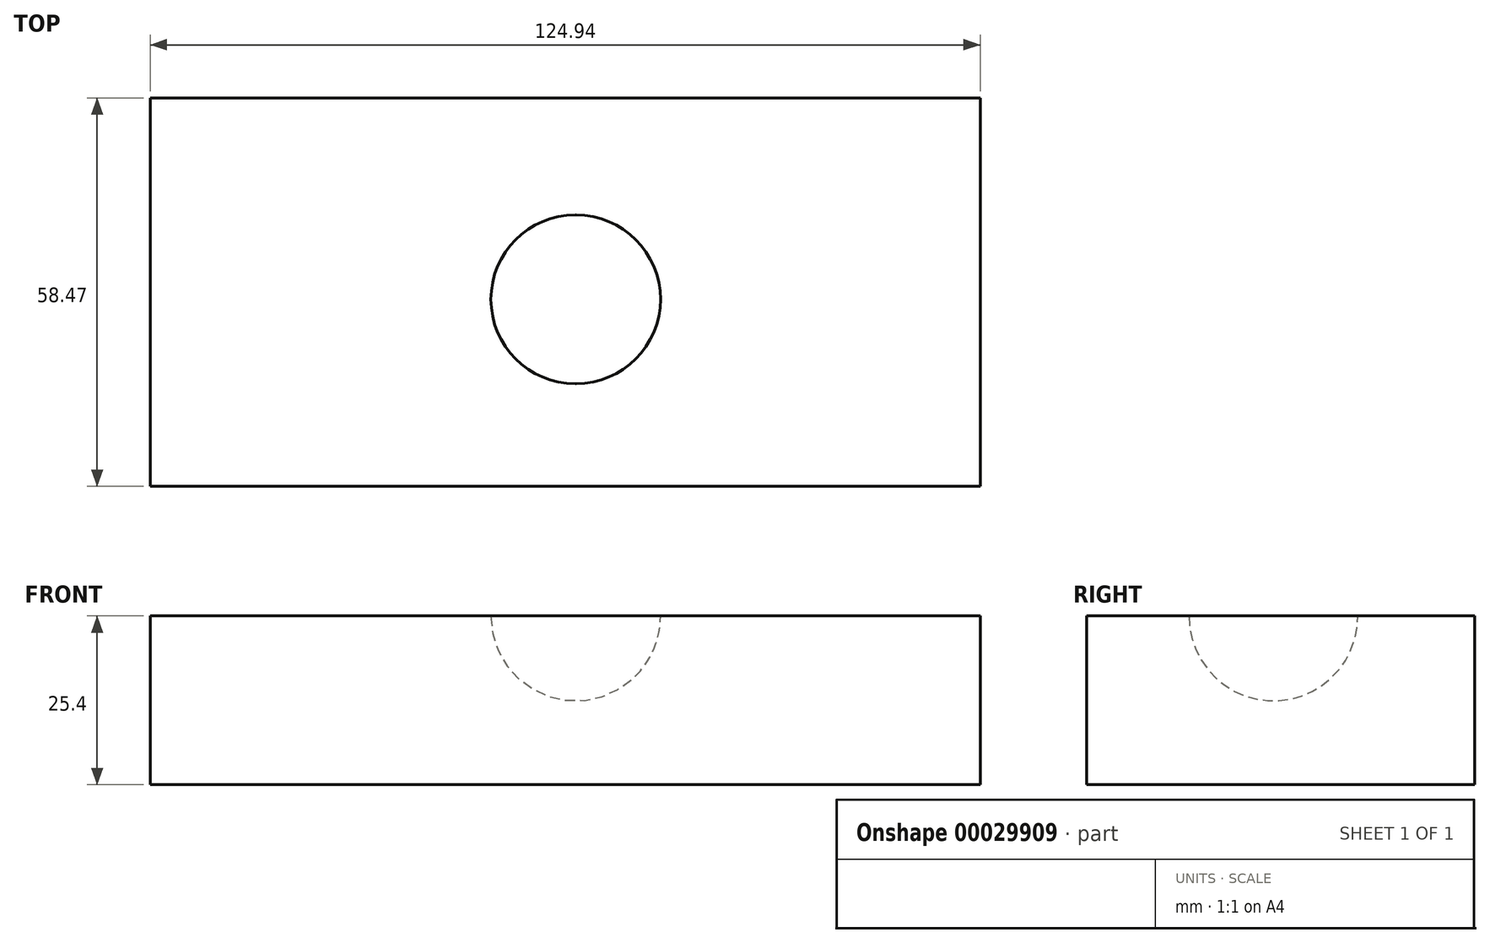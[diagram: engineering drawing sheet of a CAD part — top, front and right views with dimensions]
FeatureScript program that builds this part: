
annotation { "Feature Type Name" : "Feature", "Feature Type Description" : "" }
export const myFeature = defineFeature(function(context is Context, id is Id, definition is map)
    precondition{}
    {
        {
            var Q0;
            Q0=qCreatedBy(makeId("Top.planeOp"),FACE);
            var sketch = newSketch(context, id + "F0", { "sketchPlane" : qUnion([Q0])});
            skLineSegment(sketch, "E0.bottom", {"start": v(-64.04, 28.95) * mm, "end": v(60.9, 28.95) * mm});
            skLineSegment(sketch, "E0.top", {"start": v(-64.04, -29.52) * mm, "end": v(60.9, -29.52) * mm});
            skLineSegment(sketch, "E0.left", {"start": v(-64.04, 28.95) * mm, "end": v(-64.04, -29.52) * mm});
            skLineSegment(sketch, "E0.right", {"start": v(60.9, 28.95) * mm, "end": v(60.9, -29.52) * mm});
            skSolve(sketch);
        }
        {
            var Q0;
            Q0=makeQuery(id+"F0.imprint","IMPRINT",FACE,{"disambiguationData":[TD([[makeQuery(id+"F0.imprint","IMPRINT",EDGE,{"derivedFrom":sQuery(id+"F0.wireOp",EDGE,"E0.bottom")}),-1.0]])]});
            extrude(context, id + "F1", {"entities" : qUnion([Q0]), "depth" : 25.4 * mm});
        }
        {
            var Q0;
            Q0=makeQuery(id+"F1.opExtrude","CAP_FACE",FACE,{"disambiguationData":[OSD([sQuery(id+"F0.wireOp",EDGE,"E0.bottom"),sQuery(id+"F0.wireOp",EDGE,"E0.top"),sQuery(id+"F0.wireOp",EDGE,"E0.left"),sQuery(id+"F0.wireOp",EDGE,"E0.right")])],"isStart":false});
            var sketch = newSketch(context, id + "F2", { "sketchPlane" : qUnion([Q0])});
            skLineSegment(sketch, "E1", {"start": v(0, 11.33) * mm, "end": v(0, -14.07) * mm});
            skArc(sketch, "E2", {"start": v(0, 11.33) * mm, "mid": v(-12.77, -1.37) * mm, "end": v(0, -14.07) * mm});
            skSolve(sketch);
        }
        {
            var Q0;
            Q0=makeQuery(id+"F2.imprint","IMPRINT",FACE,{"disambiguationData":[TD([[makeQuery(id+"F2.imprint","IMPRINT",EDGE,{"derivedFrom":sQuery(id+"F2.wireOp",EDGE,"E1")}),-1.0]])]});
            var Q1;
            Q1=sQuery(id+"F2.wireOp",EDGE,"E1");
            revolve(context, id + "F3", {"operationType" : NewBodyOperationType.REMOVE, "entities" : qUnion([Q0]), "axis" : qUnion([Q1]), "revolveType" : RevolveType.FULL, "oppositeDirection" : true});
        }
    });
